# Revit family: TSL_US - TSLNANO - The Nano Sink
name_source: partatom
category: Plumbing Fixtures
units: mm (PartAtom-declared; Revit-internal decimal feet)

## family parameters
Always vertical = Yes
Cut with Voids When Loaded = No
Part Type = Normal
Room Calculation Point = No
Round Connector Dimension = Use Diameter
Shared = No
Work Plane-Based = No

## types (1)
- TSL.NANO - White
    Assembly Code = D2010400
    Default Elevation = 0' - 0"
    Description = A 20” wide compact wash basin constructed in solid surface with concealed waste and 1 1/4” waste connection. Includes steel supporting wall bracket.
    Keynote = 22 40 00.A7
    Manufacturer = The Splash Lab
    Model = TSL.NANO.WH
    TSL Connector Diameter = 0' - 1 1/4"
    TSL Depth = 1' - 5"
    TSL Height = 0' - 5"
    TSL Material 01 = TSL - Material - Glacier White
    TSL Material 02 = TSL - Material - Stainless Steel
    TSL Width = 1' - 8"
    Type Comments = THE NANO SINK
    Type Image = <None>
    URL = https://thesplashlab.com

## geometry (parser evidence)
native form markers: Sweep x20
no freeform markers — native parametric forms only
